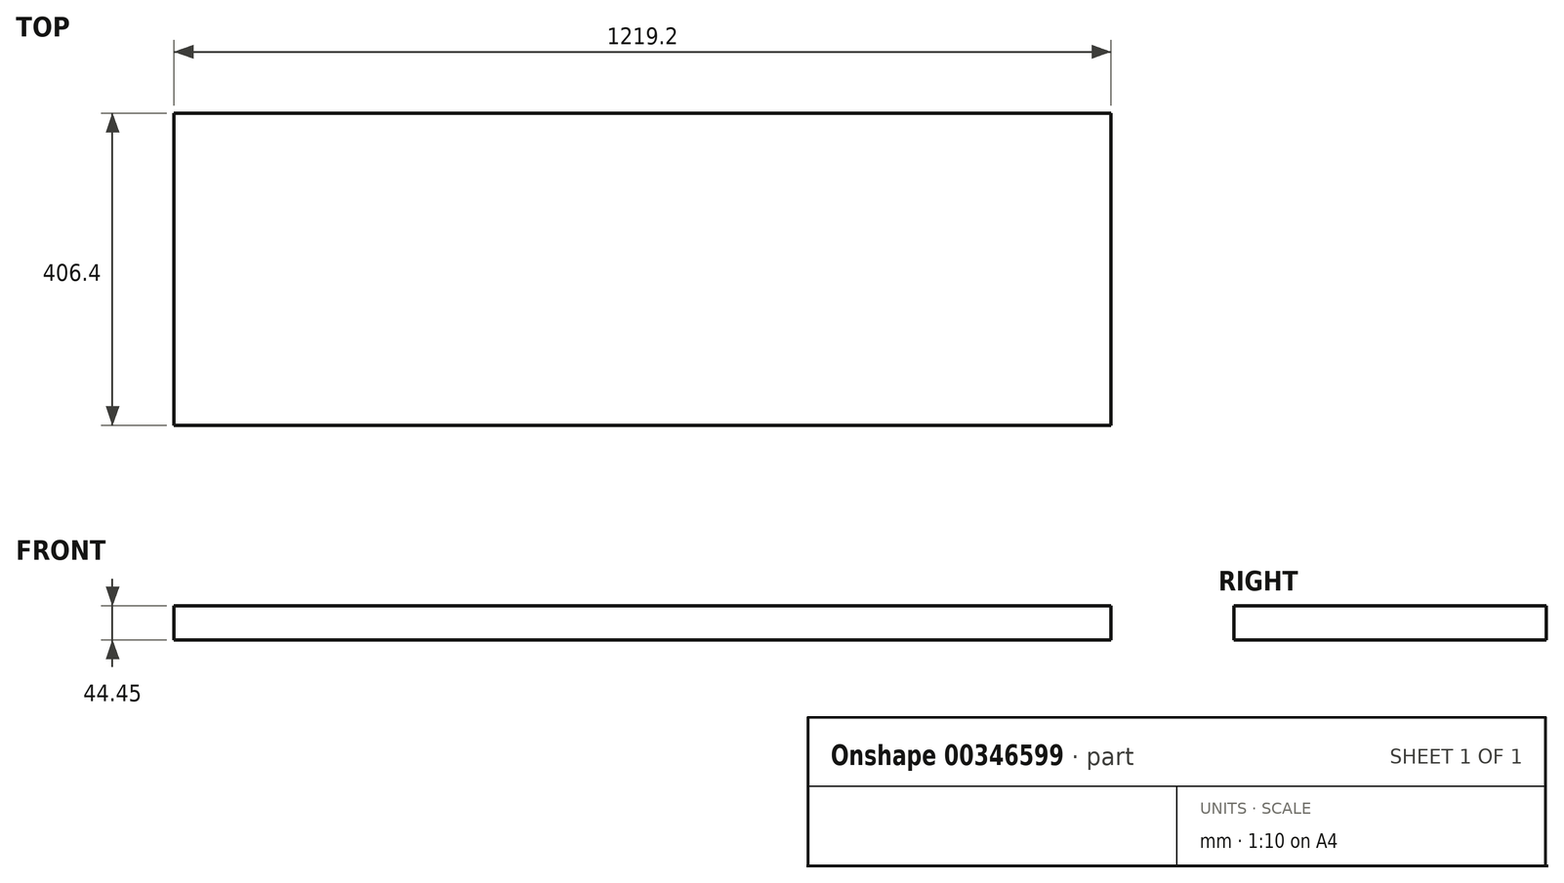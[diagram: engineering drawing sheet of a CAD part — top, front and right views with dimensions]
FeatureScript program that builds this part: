
annotation { "Feature Type Name" : "Feature", "Feature Type Description" : "" }
export const myFeature = defineFeature(function(context is Context, id is Id, definition is map)
    precondition{}
    {
        {
            var Q0;
            Q0=qCreatedBy(makeId("Top.planeOp"),FACE);
            var sketch = newSketch(context, id + "F0", { "sketchPlane" : qUnion([Q0])});
            skLineSegment(sketch, "E0.bottom", {"start": v(609.6, -203.2) * mm, "end": v(-609.6, -203.2) * mm});
            skLineSegment(sketch, "E0.top", {"start": v(609.6, 203.2) * mm, "end": v(-609.6, 203.2) * mm});
            skLineSegment(sketch, "E0.left", {"start": v(609.6, -203.2) * mm, "end": v(609.6, 203.2) * mm});
            skLineSegment(sketch, "E0.right", {"start": v(-609.6, -203.2) * mm, "end": v(-609.6, 203.2) * mm});
            skPoint(sketch, "E0.middle", {"position": v(0, 0) * mm});
            skSolve(sketch);
        }
        {
            var Q0;
            Q0 = qSketchRegion(id + "F0", true);
            extrude(context, id + "F1", {"entities" : qUnion([Q0]), "depth" : 44.45 * mm});
        }
    });
